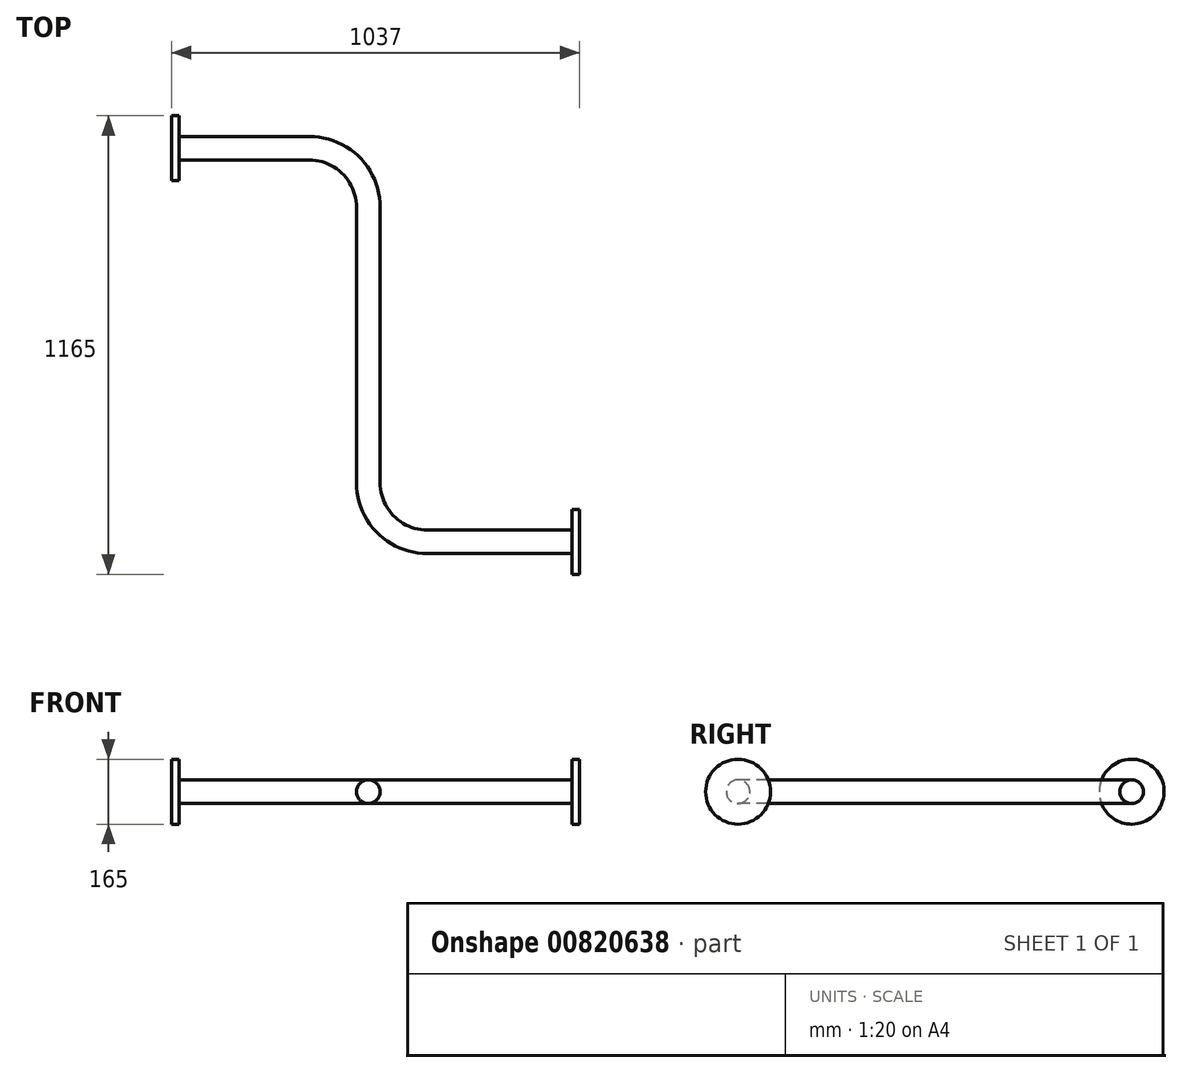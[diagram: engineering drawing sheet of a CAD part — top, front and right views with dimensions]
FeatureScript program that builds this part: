
annotation { "Feature Type Name" : "Feature", "Feature Type Description" : "" }
export const myFeature = defineFeature(function(context is Context, id is Id, definition is map)
    precondition{}
    {
        {
            var Q0;
            Q0=qCreatedBy(makeId("Top.planeOp"),FACE);
            var sketch = newSketch(context, id + "F0", { "sketchPlane" : qUnion([Q0])});
            skLineSegment(sketch, "E0", {"start": v(0, 0) * mm, "end": v(350, 0) * mm});
            skLineSegment(sketch, "E1", {"start": v(500, -150) * mm, "end": v(500, -850) * mm});
            skLineSegment(sketch, "E2", {"start": v(650, -1000) * mm, "end": v(1037, -1000) * mm});
            skPoint(sketch, "E3.visualSharp", {"position": v(500, 0) * mm});
            skArc(sketch, "E3.filletArc", {"start": v(500, -150) * mm, "mid": v(456.07, -43.93) * mm, "end": v(350, 0) * mm});
            skPoint(sketch, "E4.visualSharp", {"position": v(500, -1000) * mm});
            skArc(sketch, "E4.filletArc", {"start": v(500, -850) * mm, "mid": v(543.93, -956.07) * mm, "end": v(650, -1000) * mm});
            skSolve(sketch);
        }
        {
            var Q0;
            Q0=qCreatedBy(makeId("Right.planeOp"),FACE);
            var sketch = newSketch(context, id + "F1", { "sketchPlane" : qUnion([Q0])});
            skCircle(sketch, "E5", {"center": v(0, 0) * mm, "radius": 30 * mm});
            skCircle(sketch, "E6", {"center": v(0, 0) * mm, "radius": 82.5 * mm});
            skSolve(sketch);
        }
        {
            var Q0;
            Q0=makeQuery(id+"F1.imprint","IMPRINT",FACE,{"disambiguationData":[TD([[makeQuery(id+"F1.imprint","IMPRINT",EDGE,{"derivedFrom":sQuery(id+"F1.wireOp",EDGE,"E5")}),1.0]])]});
            var Q1;
            Q1=sQuery(id+"F0.wireOp",EDGE,"E0");
            var Q2;
            Q2=sQuery(id+"F0.wireOp",EDGE,"E3.filletArc");
            var Q3;
            Q3=sQuery(id+"F0.wireOp",EDGE,"E1");
            var Q4;
            Q4=sQuery(id+"F0.wireOp",EDGE,"E4.filletArc");
            var Q5;
            Q5=sQuery(id+"F0.wireOp",EDGE,"E2");
            sweep(context, id + "F2", {"profiles" : qUnion([Q0]), "path" : qUnion([Q1, Q2, Q3, Q4, Q5])});
        }
        {
            var Q0;
            Q0=makeQuery(id+"F1.imprint","IMPRINT",FACE,{"disambiguationData":[TD([[makeQuery(id+"F1.imprint","IMPRINT",EDGE,{"derivedFrom":sQuery(id+"F1.wireOp",EDGE,"E5")}),-1.0]])]});
            extrude(context, id + "F3", {"entities" : qUnion([Q0]), "operationType" : NewBodyOperationType.ADD, "depth" : 20 * mm, "offsetDistance" : 25 * mm});
        }
        {
            var Q0;
            Q0=makeQuery(id+"F2.opSweep","CAP_FACE",FACE,{"disambiguationData":[OSD([sQuery(id+"F0.wireOp",VERTEX,"E2.end"),sQuery(id+"F1.wireOp",EDGE,"E5")])],"isStart":false});
            var sketch = newSketch(context, id + "F4", { "sketchPlane" : qUnion([Q0])});
            skCircle(sketch, "E7", {"center": v(-1000, 0) * mm, "radius": 82.5 * mm});
            skSolve(sketch);
        }
        {
            var Q0;
            Q0=makeQuery(id+"F4.imprint","IMPRINT",FACE,{"disambiguationData":[TD([[makeQuery(id+"F4.imprint","IMPRINT",EDGE,{"derivedFrom":sQuery(id+"F4.wireOp",EDGE,"E7")}),1.0]])]});
            extrude(context, id + "F5", {"entities" : qUnion([Q0]), "operationType" : NewBodyOperationType.ADD, "oppositeDirection" : true, "depth" : 20 * mm, "offsetDistance" : 25 * mm});
        }
    });
